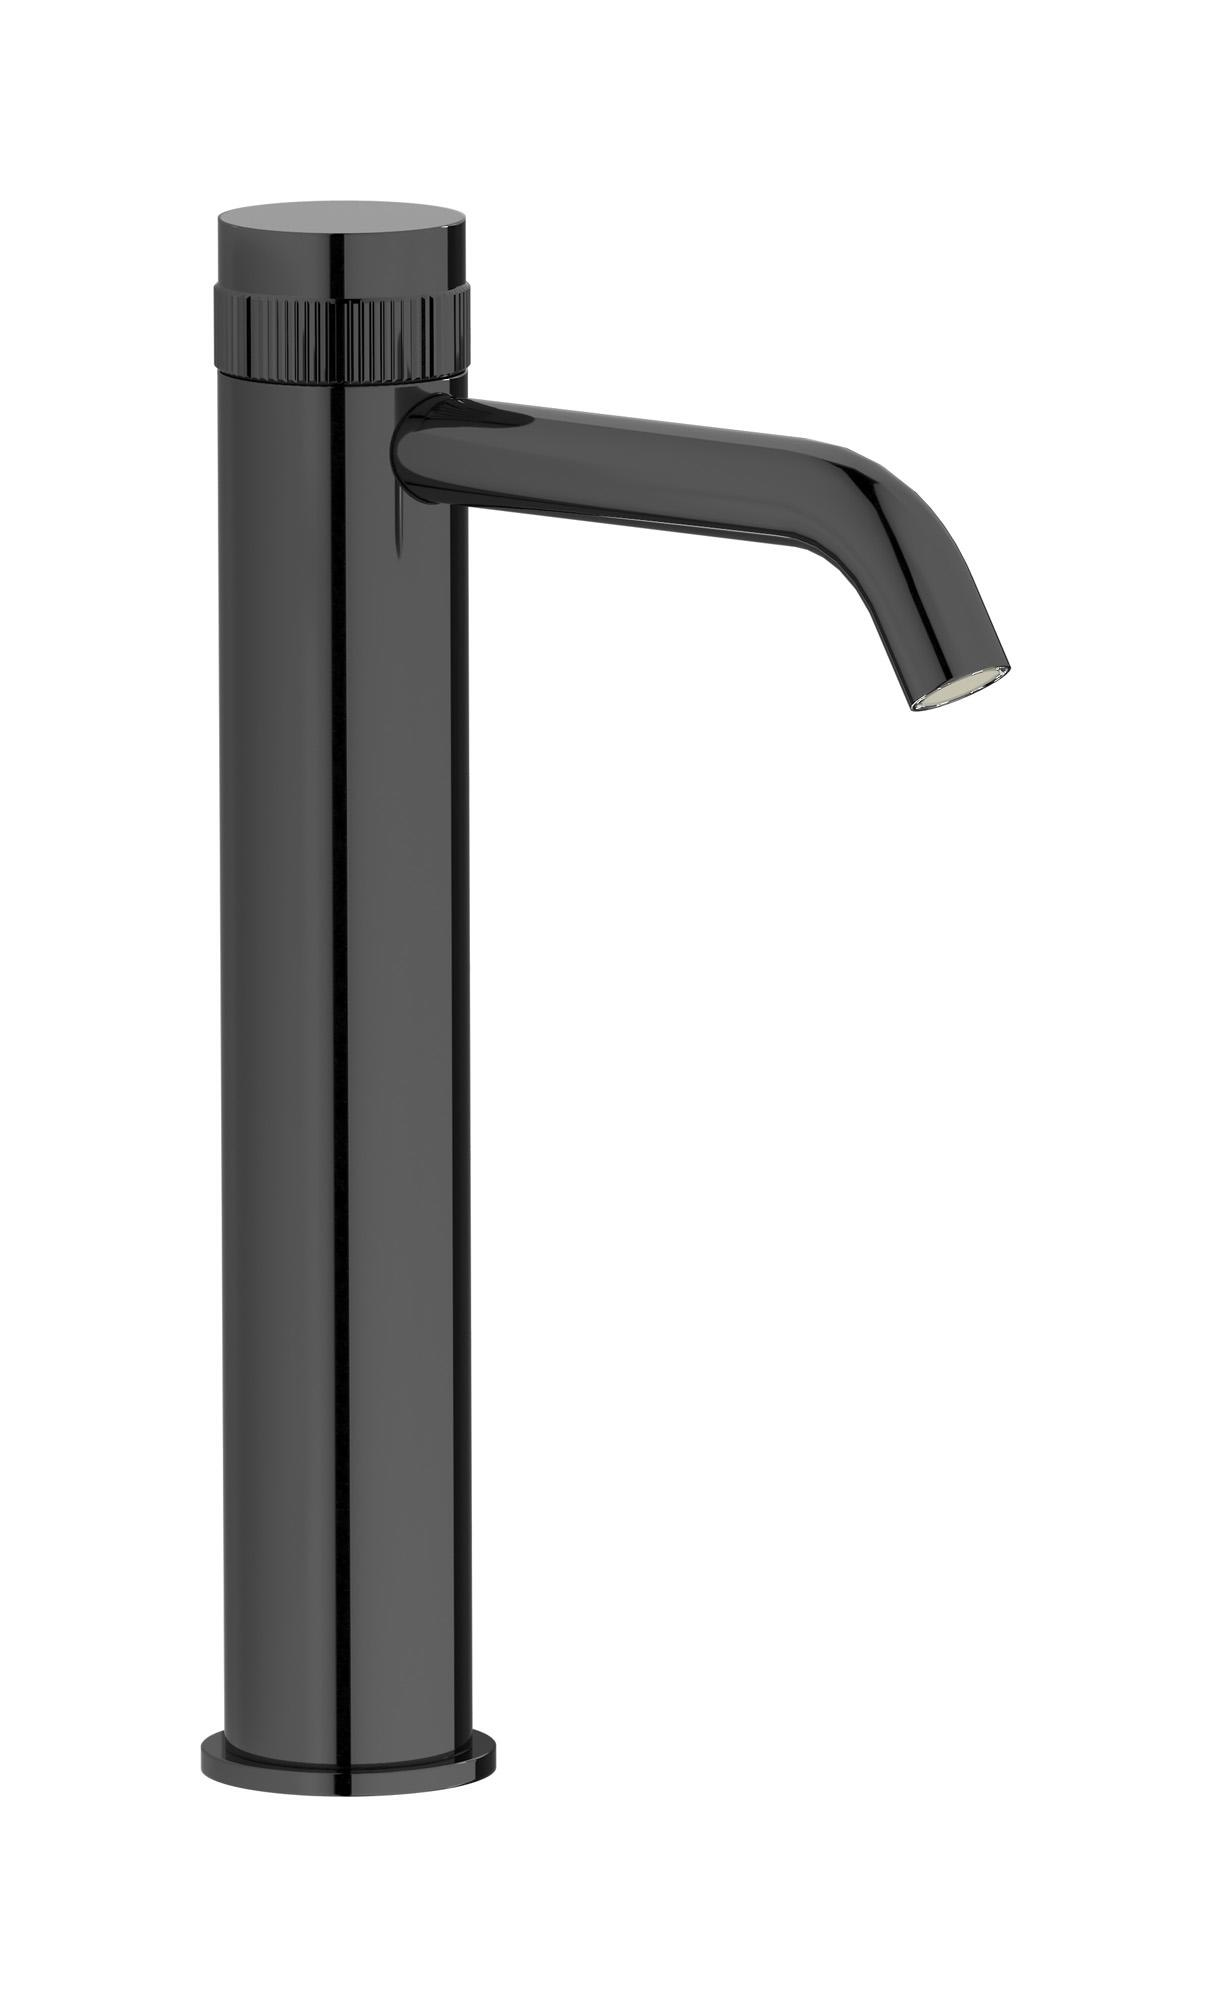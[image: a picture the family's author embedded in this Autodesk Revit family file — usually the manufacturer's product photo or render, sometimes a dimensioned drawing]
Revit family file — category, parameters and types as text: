
# Revit family: RX202
name_source: partatom
category: Apparecchi idraulici
units: mm (PartAtom-declared; Revit-internal decimal feet)

## family parameters
Basato su piano di lavoro = No
Condiviso = No
Mantieni orientamento annotazione = No
Numero OmniClass = 23.45.55.17
Punto di calcolo locali = No
Quota connettore circolare = Usa diametro
Sempre verticale = Sì
Taglio con vuoti quando caricato = No
Tipo di parte = Normale
Titolo OmniClass = Mixing Faucets

## types (12) — shared parameters
Cold water inlet = 10 mm  [stored 0.0328084 ft]
Commenti sul tipo = Tall monohole washbasin hydroprogressive mixer complete with drain
Connessione CW = No
Connessione HW = No
Connessione di scarico = No
Connessione di ventilazione = No
Descrizione = Tall monohole washbasin hydroprogressive mixer complete with drain
Hot water inlet = 10 mm  [stored 0.0328084 ft]
Produttore = IB Rubinetterie S.p.A.
URL = https://www.weareib.it
zero-valued in all types: Prospetto di default

## per-type parameters (varying)
| type | Finishes surface | Immagine tipo | Modello |
| Chrome | IB_Chrome | RX202CC.jpg | RX202CC |
| Black Chrome | IB_Black chrome | RX202CF.jpg | RX202CF |
| Brushed Black Chrome | IB_Brushed black chrome | RX202CS.jpg | RX202CS |
| Pale Gold | IB_Pale gold | RX202II.jpg | RX202II |
| Brushed Pale Gold | IB_brushed pale gold | RX202IS.jpg | RX202IS |
| Matt Black | IB_matt black | RX202NP.jpg | RX202NP |
| Natural Brass | IB_Brass | RX202ON.jpg | RX202ON |
| Gold | IB_gold | RX202OO.jpg | RX202OO |
| Brushed Gold | IB_brushed gold | RX202OS.jpg | RX202OS |
| Rose Gold | IB_Rose gold | RX202RS.jpg | RX202RS |
| Brushed Rose Gold | IB_Brushed rose gold | RX202SR.jpg | RX202SR |
| Brushed Nickel | IB_Brushed nickel | RX202SS.jpg | RX202SS |

note: [stored X ft] marks values corroborated as IEEE doubles in the binary element streams (Revit-internal decimal feet)
